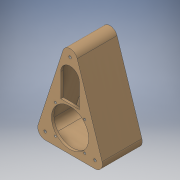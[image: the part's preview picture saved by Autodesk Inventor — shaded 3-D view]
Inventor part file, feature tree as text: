
AUTODESK INVENTOR PART (.ipt)
format: ipt  version: 2016 (Build 200138000, 138)  size: 229,888 bytes
history: native  units: in
note: dims shown in document units (in); Inventor stores cm internally (conversion verified against a paired STEP export)
features: extrude x4, sketch x4
ambient origin geometry x8: Origin, YZ Plane, XZ Plane, XY Plane, X Axis, Y Axis, Z Axis, Center Point
bodies: Body1 (feature_tree)
feature tree (8):
  extrude  "Extrusion2"  Depth=0.5in
  extrude  "Extrusion3"  Depth=0.5in
  extrude  "Extrusion4"  Depth=0.2469in
  extrude  "Extrusion5"  Depth=0.5in
  sketch  "Sketch1"  dims[d7=1.0in d9=0.5in]
  sketch  "Sketch2"  dims[d10=0.5in d11=0.5in]
  sketch  "Sketch3"  dims[d14=4.0in d15=0.2469in]
  sketch  "Sketch4"  dims[d16=0.495in d17=0.5in d18=6.6667in d19=4.3049in d20=6.4829in d21=6.4829in d29=0.25in d30=3.0in d33=0.166in d34=0.166in d35=0.166in d36=0.166in d50=0.15in d51=0.75in d52=0.75in d53=1.9in d54=1.9in d55=0.2in d56=0.0in d57=1.2in d58=1.2in d59=1.2in d60=2.8in d61=0.2in d62=0.0in d63=0.0in d64=0.2in d65=0.0in d66=0.2in d67=0.2in d68=0.2in d69=3.2in d70=0.0in]
